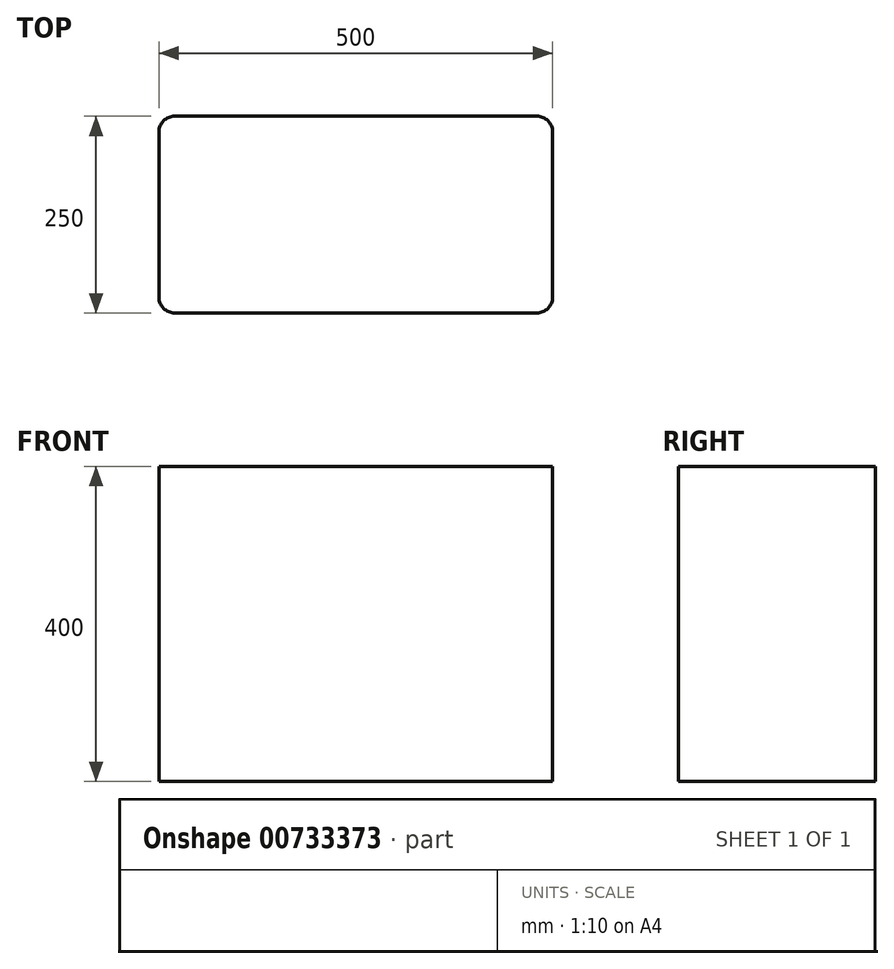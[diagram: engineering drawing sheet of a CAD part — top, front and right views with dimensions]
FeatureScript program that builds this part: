
annotation { "Feature Type Name" : "Feature", "Feature Type Description" : "" }
export const myFeature = defineFeature(function(context is Context, id is Id, definition is map)
    precondition{}
    {
        {
            var Q0;
            Q0=qCreatedBy(makeId("Top.planeOp"),FACE);
            var sketch = newSketch(context, id + "F0", { "sketchPlane" : qUnion([Q0])});
            skLineSegment(sketch, "E0.bottom", {"start": v(-230, -125) * mm, "end": v(230, -125) * mm});
            skLineSegment(sketch, "E0.top", {"start": v(-230, 125) * mm, "end": v(230, 125) * mm});
            skLineSegment(sketch, "E0.left", {"start": v(-250, -105) * mm, "end": v(-250, 105) * mm});
            skLineSegment(sketch, "E0.right", {"start": v(250, -105) * mm, "end": v(250, 105) * mm});
            skPoint(sketch, "E0.middle", {"position": v(0, 0) * mm});
            skPoint(sketch, "E1.visualSharp", {"position": v(-250, -125) * mm});
            skArc(sketch, "E1.filletArc", {"start": v(-250, -105) * mm, "mid": v(-244.14, -119.14) * mm, "end": v(-230, -125) * mm});
            skPoint(sketch, "E2.visualSharp", {"position": v(-250, 125) * mm});
            skArc(sketch, "E2.filletArc", {"start": v(-230, 125) * mm, "mid": v(-244.14, 119.14) * mm, "end": v(-250, 105) * mm});
            skPoint(sketch, "E3.visualSharp", {"position": v(250, 125) * mm});
            skArc(sketch, "E3.filletArc", {"start": v(250, 105) * mm, "mid": v(244.14, 119.14) * mm, "end": v(230, 125) * mm});
            skPoint(sketch, "E4.visualSharp", {"position": v(250, -125) * mm});
            skArc(sketch, "E4.filletArc", {"start": v(230, -125) * mm, "mid": v(244.14, -119.14) * mm, "end": v(250, -105) * mm});
            skSolve(sketch);
        }
        {
            var Q0;
            Q0=makeQuery(id+"F0.imprint","IMPRINT",FACE,{"disambiguationData":[TD([[makeQuery(id+"F0.imprint","IMPRINT",EDGE,{"derivedFrom":sQuery(id+"F0.wireOp",EDGE,"E0.bottom")}),1.0]])]});
            extrude(context, id + "F1", {"entities" : qUnion([Q0]), "depth" : 400 * mm, "offsetDistance" : 25 * mm});
        }
    });
